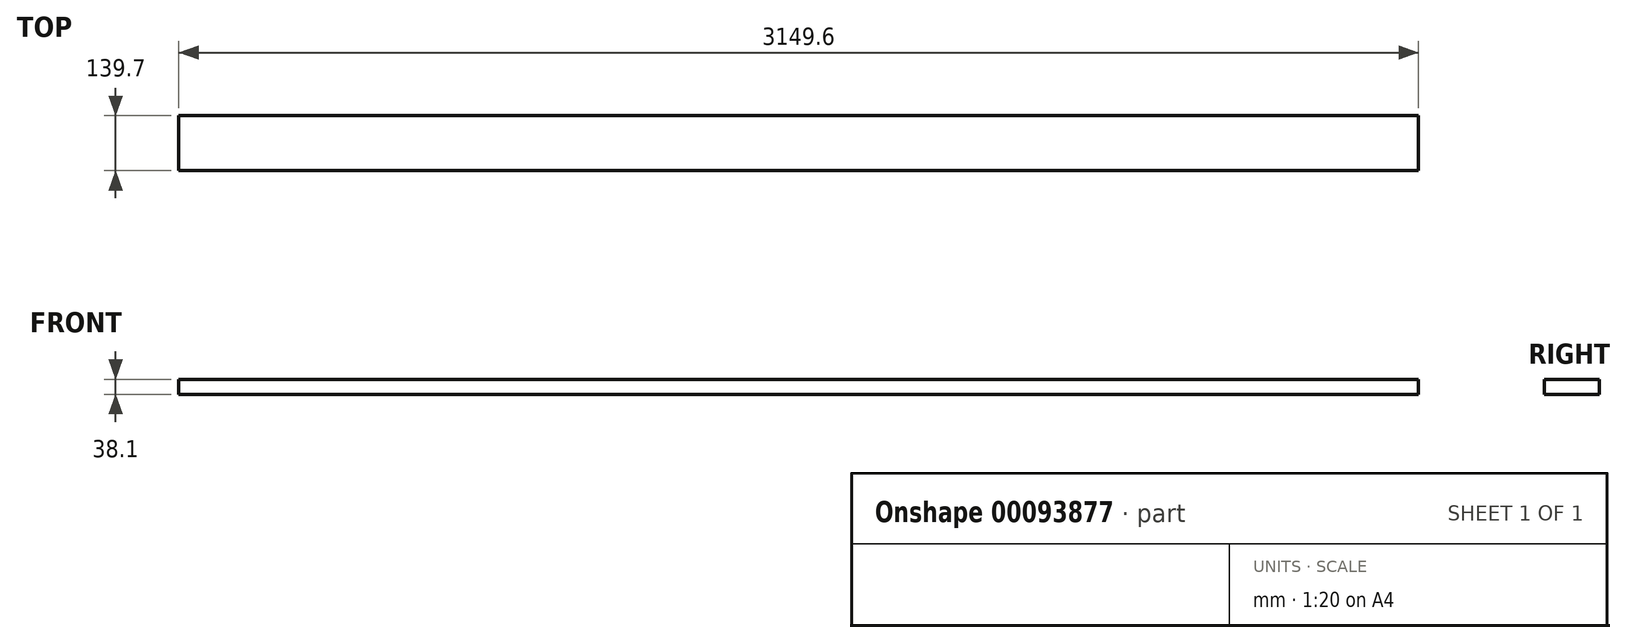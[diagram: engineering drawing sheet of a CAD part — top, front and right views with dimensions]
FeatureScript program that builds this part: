
annotation { "Feature Type Name" : "Feature", "Feature Type Description" : "" }
export const myFeature = defineFeature(function(context is Context, id is Id, definition is map)
    precondition{}
    {
        {
            var Q0;
            Q0=qCreatedBy(makeId("Top.planeOp"),FACE);
            var sketch = newSketch(context, id + "F0", { "sketchPlane" : qUnion([Q0])});
            skLineSegment(sketch, "E0.bottom", {"start": v(-1574.8, 139.7) * mm, "end": v(1574.8, 139.7) * mm});
            skLineSegment(sketch, "E0.top", {"start": v(-1574.8, 0) * mm, "end": v(1574.8, 0) * mm});
            skLineSegment(sketch, "E0.left", {"start": v(-1574.8, 139.7) * mm, "end": v(-1574.8, 0) * mm});
            skLineSegment(sketch, "E0.right", {"start": v(1574.8, 139.7) * mm, "end": v(1574.8, 0) * mm});
            skSolve(sketch);
        }
        {
            var Q0;
            Q0=qSketchRegion(id+"F0",true);
            extrude(context, id + "F1", {"entities" : qUnion([Q0]), "depth" : 38.1 * mm});
        }
    });
